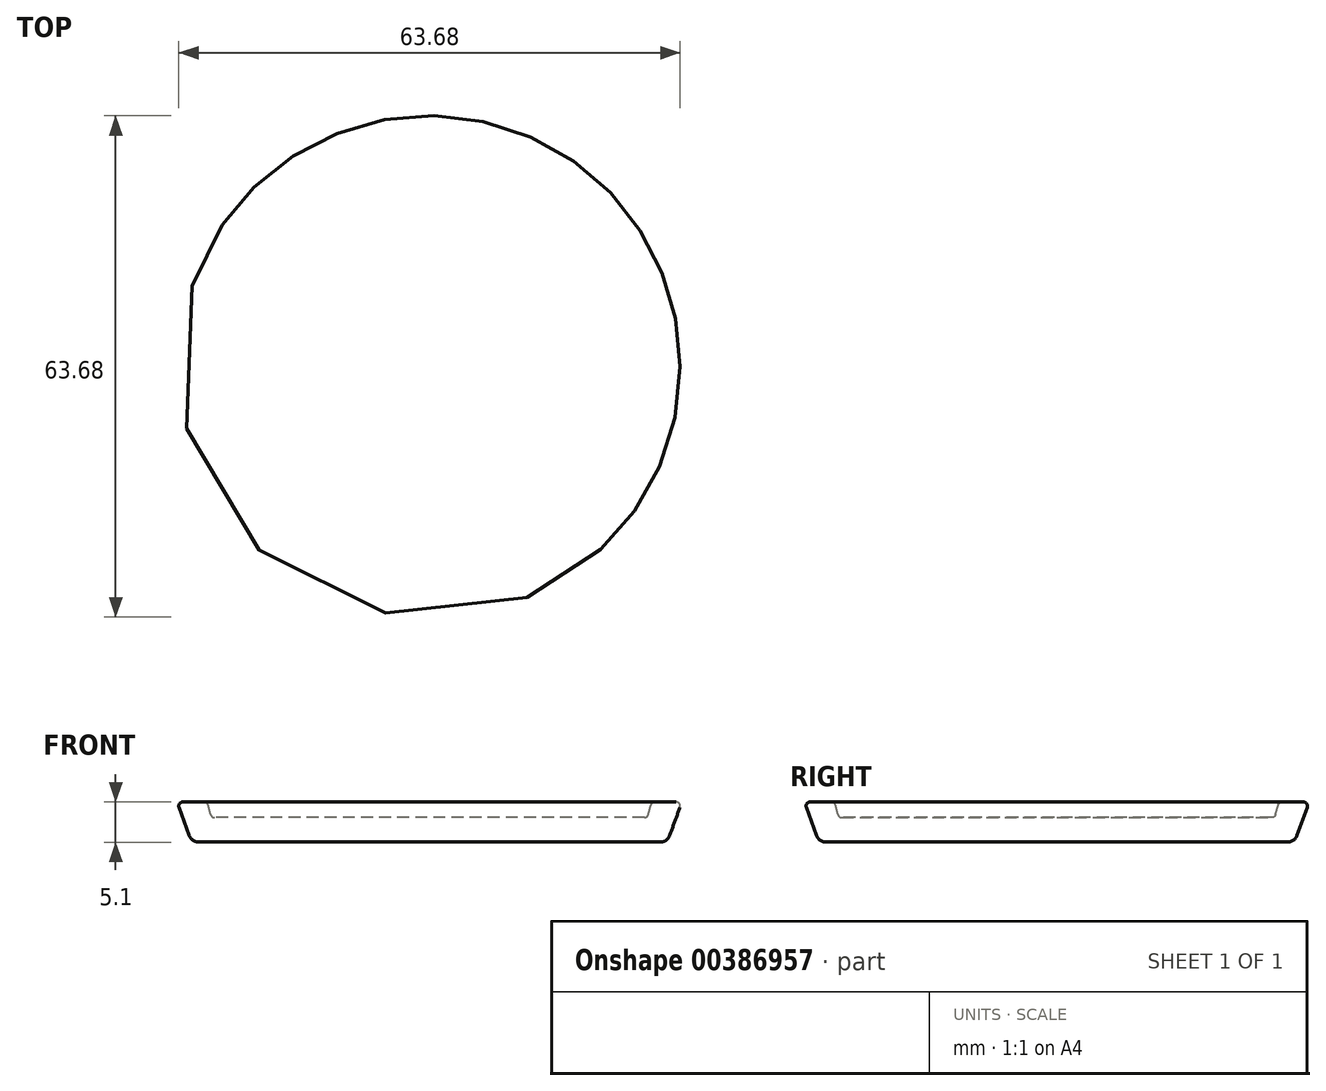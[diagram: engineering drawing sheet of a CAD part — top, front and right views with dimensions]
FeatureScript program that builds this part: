
annotation { "Feature Type Name" : "Feature", "Feature Type Description" : "" }
export const myFeature = defineFeature(function(context is Context, id is Id, definition is map)
    precondition{}
    {
        {
            var Q0;
            Q0=qCreatedBy(makeId("Front.planeOp"),FACE);
            var sketch = newSketch(context, id + "F0", { "sketchPlane" : qUnion([Q0])});
            skLineSegment(sketch, "E0", {"start": v(0, 7.6) * mm, "end": v(27.3, 7.6) * mm});
            skLineSegment(sketch, "E1", {"start": v(27.8, 7.98) * mm, "end": v(28.12, 9.2) * mm});
            skLineSegment(sketch, "E2", {"start": v(28.62, 9.58) * mm, "end": v(31.34, 9.58) * mm});
            skLineSegment(sketch, "E3", {"start": v(31.81, 8.9) * mm, "end": v(30.51, 5.32) * mm});
            skLineSegment(sketch, "E4", {"start": v(29.32, 4.48) * mm, "end": v(0, 4.48) * mm});
            skPoint(sketch, "E5.visualSharp", {"position": v(27.7, 7.6) * mm});
            skArc(sketch, "E5.filletArc", {"start": v(27.3, 7.6) * mm, "mid": v(27.61, 7.7) * mm, "end": v(27.8, 7.98) * mm});
            skPoint(sketch, "E6.visualSharp", {"position": v(28.23, 9.58) * mm});
            skArc(sketch, "E6.filletArc", {"start": v(28.62, 9.58) * mm, "mid": v(28.3, 9.48) * mm, "end": v(28.12, 9.2) * mm});
            skPoint(sketch, "E7.visualSharp", {"position": v(32.06, 9.58) * mm});
            skArc(sketch, "E7.filletArc", {"start": v(31.81, 8.9) * mm, "mid": v(31.75, 9.36) * mm, "end": v(31.34, 9.58) * mm});
            skPoint(sketch, "E8.visualSharp", {"position": v(30.2, 4.48) * mm});
            skArc(sketch, "E8.filletArc", {"start": v(29.32, 4.48) * mm, "mid": v(30.05, 4.71) * mm, "end": v(30.51, 5.32) * mm});
            skLineSegment(sketch, "E9", {"start": v(0, 7.6) * mm, "end": v(0, 4.48) * mm});
            skSolve(sketch);
        }
        {
            var Q0;
            Q0=qCreatedBy(makeId("Front.planeOp"),FACE);
            var sketch = newSketch(context, id + "F1", { "sketchPlane" : qUnion([Q0])});
            skLineSegment(sketch, "E10", {"start": v(0, 8.96) * mm, "end": v(0, 1.1) * mm});
            skSolve(sketch);
        }
        {
            var Q0;
            Q0 = qSketchRegion(id + "F0", true);
            var Q1;
            Q1=sQuery(id+"F1.wireOp",EDGE,"E10");
            revolve(context, id + "F2", {"entities" : qUnion([Q0]), "axis" : qUnion([Q1]), "revolveType" : RevolveType.FULL});
        }
    });
